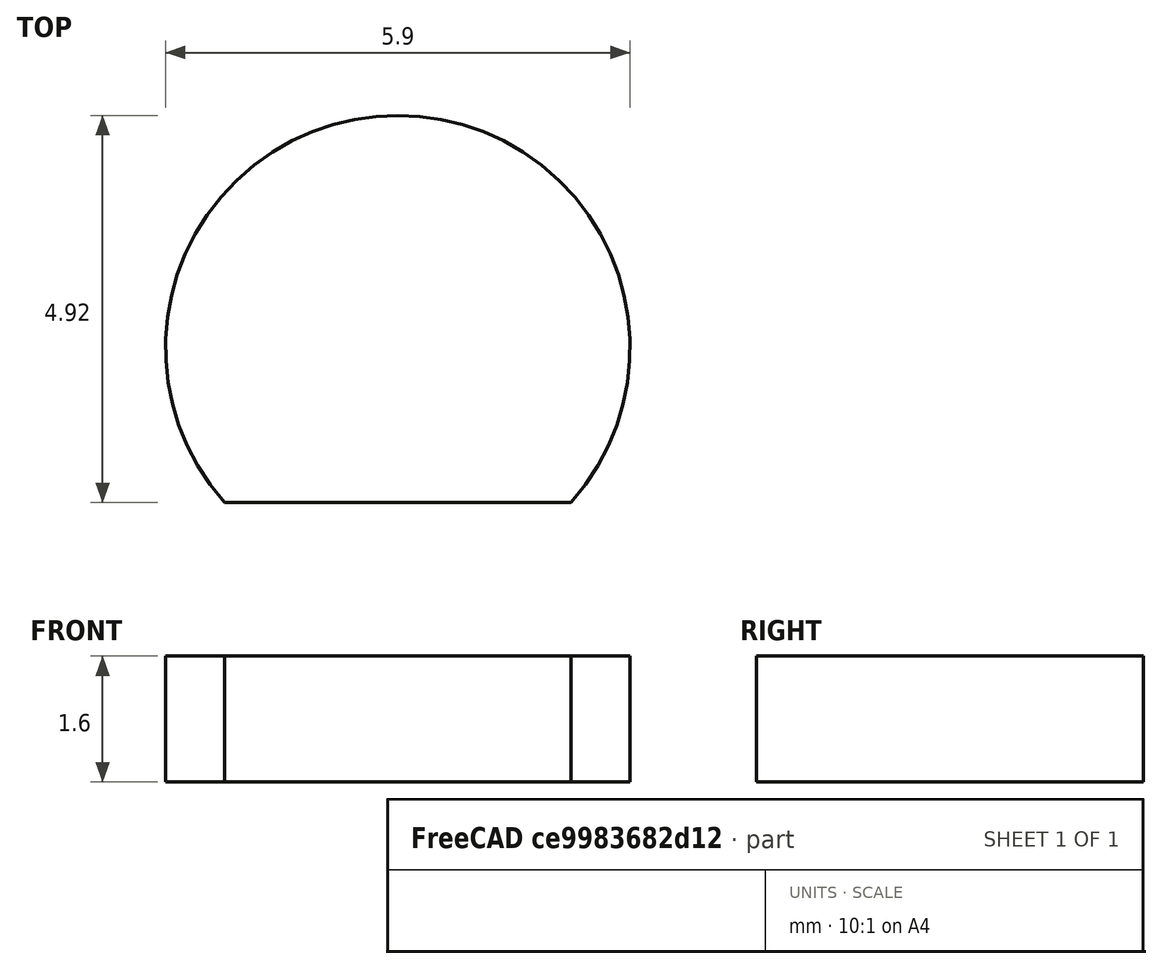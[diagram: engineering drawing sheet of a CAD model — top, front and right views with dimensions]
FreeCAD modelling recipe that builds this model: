
FCSTD DOCUMENT  (FreeCAD 0.18R15969 (Git))
Label: potcap-insert
License: All rights reserved
LicenseURL: http://en.wikipedia.org/wiki/All_rights_reserved
objects: TechDraw::DrawViewDimension×4, TechDraw::DrawProjGroupItem×3, TechDraw::DrawProjGroup×2, Sketcher::SketchObject×1, PartDesign::Pad×1, PartDesign::Body×1, TechDraw::DrawSVGTemplate×1, TechDraw::DrawViewAnnotation×1, TechDraw::DrawPage×1
note: 4 computed .brp shape members not serialized (recipe doc carries the construction recipe); baked Part::Feature solids carry a one-line shape summary decoded from their .brp

FEATURE [Sketcher::SketchObject] Sketch
  MapMode = 5
  Support = -> [XY_Plane]
  sketch-geometry (2):
    g0: ArcOfCircle CenterX=0 CenterY=0 CenterZ=0 NormalX=0 NormalY=0 NormalZ=1 AngleXU=0 Radius=2.95 StartAngle=5.55407 EndAngle=10.1539
    g1: LineSegment StartX=-2.2 StartY=-1.96532 StartZ=0 EndX=2.2 EndY=-1.96532 EndZ=0
  constraints (6):
    c: Coincident(g0,g-1)
    c: Coincident(g1,g0)
    c: Coincident(g1,g0)
    c: Radius(g0) = 2.95
    c: DistanceX(g1,g1) = 4.4
    c: Horizontal(g1)
FEATURE [PartDesign::Pad] Pad
  Length = 1.6
  Length2 = 100
  Profile = -> Sketch
  Refine = true
  Type = 0
FEATURE [PartDesign::Body] Body
  Group = -> [Sketch,Pad]
  Origin = -> Origin
  Tip = -> Pad
FEATURE [TechDraw::DrawSVGTemplate] Template
  EditableTexts = Designed_by_Name=Suku Wc; Drawing_number=1/1; FC-Date=2019.04.29.; FC-SC=10:1; FC-SH=1/1; FC-Title=potcap-insert; Subtitle=All dimensions are in mm (millimeters); Weight=N/A
  Height = 210
  Orientation = 1
  Width = 297
FEATURE [TechDraw::DrawProjGroupItem] ProjItem  label="Front"
  CoarseView = false
  Direction = (0,0,1)
  Focus = 100
  HardHidden = false
  IsoCount = 0
  IsoHidden = false
  IsoVisible = false
  LockPosition = true
  Perspective = false
  Rotation = 0
  RotationVector = (1,0,0)
  Scale = 10
  ScaleType = 2
  SeamHidden = false
  SeamVisible = false
  SmoothHidden = false
  SmoothVisible = false
  Source = -> [Body]
  Type = 0
  X = 0
  Y = 0
FEATURE [TechDraw::DrawProjGroupItem] ProjItem002  label="Top"
  CoarseView = false
  Direction = (0,1,0)
  Focus = 100
  HardHidden = false
  IsoCount = 0
  IsoHidden = false
  IsoVisible = false
  LockPosition = false
  Perspective = false
  Rotation = 0
  RotationVector = (1,0,0)
  Scale = 10
  ScaleType = 2
  SeamHidden = false
  SeamVisible = false
  SmoothHidden = false
  SmoothVisible = false
  Source = -> [Body]
  Type = 4
  X = 0
  Y = -64.1532
FEATURE [TechDraw::DrawProjGroup] ProjGroup
  Anchor = -> ProjItem
  AutoDistribute = true
  LockPosition = false
  ProjectionType = 0
  Rotation = 0
  Scale = 10
  ScaleType = 0
  Source = -> [Body]
  Views = -> [ProjItem,ProjItem002]
  X = 76.8926
  Y = 115.751
  spacingX = 15
  spacingY = 15
FEATURE [TechDraw::DrawViewDimension] Dimension
  Arbitrary = false
  FormatSpec = %.2f
  LockPosition = false
  MeasureType = 1
  OverTolerance = 0
  References2D = -> [ProjItem002]
  Rotation = 0
  Scale = 10
  ScaleType = 0
  Type = 2
  UnderTolerance = 0
  X = -40.4478
  Y = -0.37751
FEATURE [TechDraw::DrawViewDimension] Dimension001
  Arbitrary = false
  FormatSpec = ⌀%.2f
  LockPosition = false
  MeasureType = 1
  OverTolerance = 0
  References2D = -> [ProjItem]
  Rotation = 0
  Scale = 10
  ScaleType = 0
  Type = 5
  UnderTolerance = 0
  X = 47.1745
  Y = 17.3811
FEATURE [TechDraw::DrawViewDimension] Dimension002
  Arbitrary = false
  FormatSpec = %.2f
  LockPosition = false
  MeasureType = 1
  OverTolerance = 0
  References2D = -> [ProjItem]
  Rotation = 0
  Scale = 10
  ScaleType = 0
  Type = 1
  UnderTolerance = 0
  X = -1.13253
  Y = -34.3919
FEATURE [TechDraw::DrawProjGroupItem] ProjItem003  label="Front001"
  CoarseView = false
  Direction = (0.577,-0.577,0.577)
  Focus = 100
  HardHidden = false
  IsoCount = 0
  IsoHidden = false
  IsoVisible = false
  LockPosition = true
  Perspective = false
  Rotation = 0
  RotationVector = (0.707,0.707,0)
  Scale = 10
  ScaleType = 2
  SeamHidden = false
  SeamVisible = false
  SmoothHidden = false
  SmoothVisible = false
  Source = -> [Pad]
  Type = 0
  X = 0
  Y = 0
FEATURE [TechDraw::DrawProjGroup] ProjGroup001
  Anchor = -> ProjItem003
  AutoDistribute = true
  LockPosition = false
  ProjectionType = 0
  Rotation = 0
  Scale = 10
  ScaleType = 0
  Source = -> [Pad]
  Views = -> [ProjItem003]
  X = 172.31
  Y = 119.124
  spacingX = 15
  spacingY = 15
FEATURE [TechDraw::DrawViewDimension] Dimension003
  Arbitrary = false
  FormatSpec = (%.2f)
  LockPosition = false
  MeasureType = 1
  OverTolerance = 0
  References2D = -> [ProjItem002]
  Rotation = 0
  Scale = 10
  ScaleType = 0
  Type = 1
  UnderTolerance = 0
  X = -1.13253
  Y = -14.4177
FEATURE [TechDraw::DrawViewAnnotation] Annotation
  Font = osifont
  LineSpace = 80
  LockPosition = false
  MaxWidth = -1
  Rotation = 0
  Scale = 10
  ScaleType = 0
  Text = Technology: Laser cut acrylic or other plastic | Material thickness: 1.6mm | Preferred panel size: 32*50 = 1600 pcs
  TextSize = 4
  TextStyle = 0
  X = 67.9213
  Y = 184.922
FEATURE [TechDraw::DrawPage] Page
  KeepUpdated = true
  ProjectionType = 0
  Scale = 10
  Template = -> Template
  Views = -> [ProjGroup,Dimension,Dimension001,Dimension002,ProjGroup001,Dimension003,Annotation]
